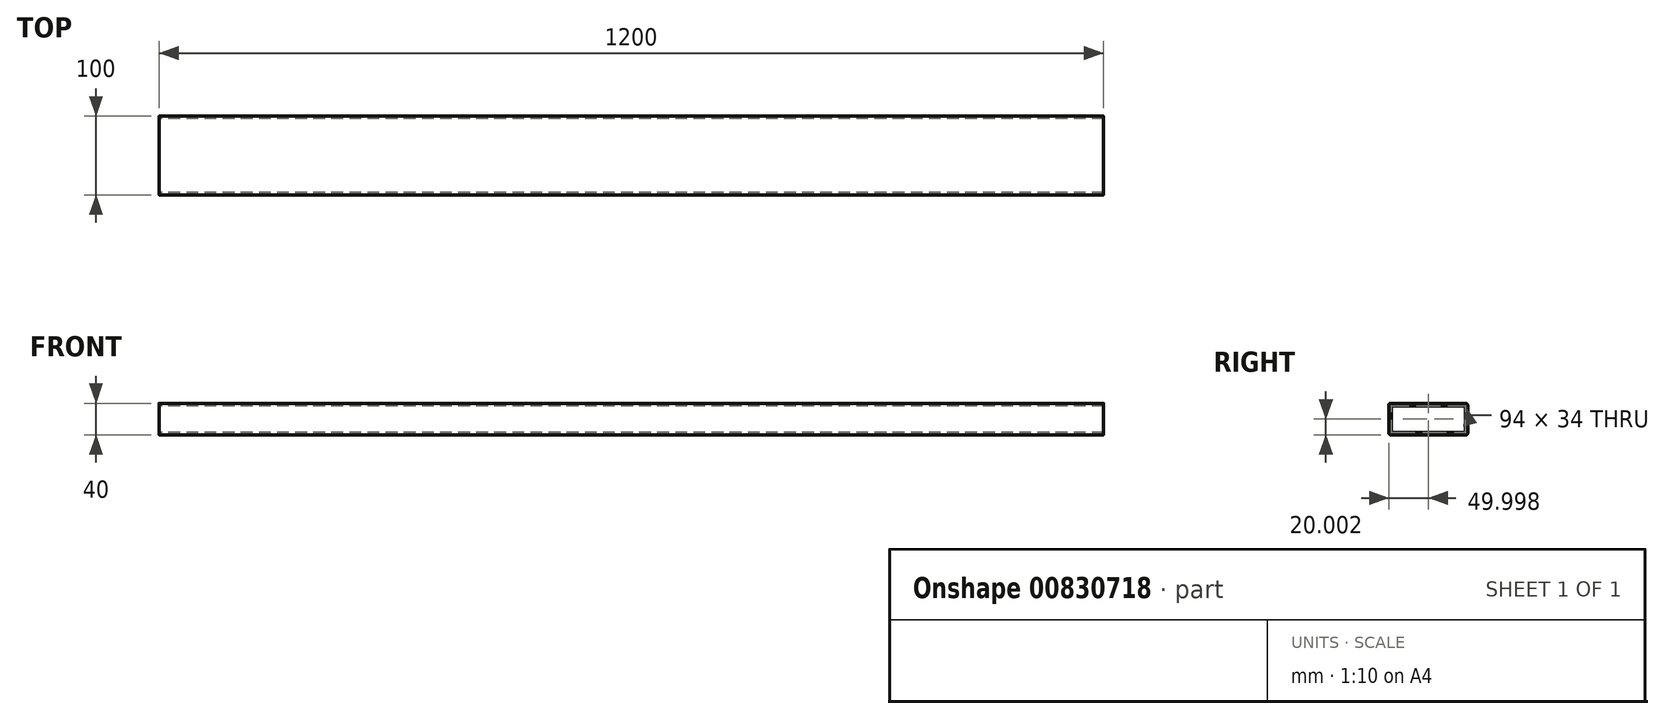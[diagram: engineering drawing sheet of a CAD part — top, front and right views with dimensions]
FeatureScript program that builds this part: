
annotation { "Feature Type Name" : "Feature", "Feature Type Description" : "" }
export const myFeature = defineFeature(function(context is Context, id is Id, definition is map)
    precondition{}
    {
        {
            assignVariable(context, id + "F0", {"name" : "LongSideSize", "anyValue" : 1200});
        }
        {
            var Q0;
            Q0=qCreatedBy(makeId("Right.planeOp"),FACE);
            var sketch = newSketch(context, id + "F1", { "sketchPlane" : qUnion([Q0])});
            skPoint(sketch, "E0.middle", {"position": v(-14.96, 34.76) * mm});
            skLineSegment(sketch, "E1.bottom", {"start": v(-17.25, -51.74) * mm, "end": v(78.75, -51.74) * mm});
            skLineSegment(sketch, "E1.top", {"start": v(-17.25, -11.74) * mm, "end": v(78.75, -11.74) * mm});
            skLineSegment(sketch, "E1.left", {"start": v(-19.25, -49.74) * mm, "end": v(-19.25, -13.74) * mm});
            skLineSegment(sketch, "E1.right", {"start": v(80.75, -49.74) * mm, "end": v(80.75, -13.74) * mm});
            skPoint(sketch, "E2.visualSharp", {"position": v(-19.25, -11.74) * mm});
            skArc(sketch, "E2.filletArc", {"start": v(-17.25, -11.74) * mm, "mid": v(-18.67, -12.32) * mm, "end": v(-19.25, -13.74) * mm});
            skPoint(sketch, "E3.visualSharp", {"position": v(80.75, -11.74) * mm});
            skArc(sketch, "E3.filletArc", {"start": v(80.75, -13.74) * mm, "mid": v(80.16, -12.32) * mm, "end": v(78.75, -11.74) * mm});
            skPoint(sketch, "E4.visualSharp", {"position": v(80.75, -51.74) * mm});
            skArc(sketch, "E4.filletArc", {"start": v(78.75, -51.74) * mm, "mid": v(80.16, -51.15) * mm, "end": v(80.75, -49.74) * mm});
            skPoint(sketch, "E5.visualSharp", {"position": v(-19.25, -51.74) * mm});
            skArc(sketch, "E5.filletArc", {"start": v(-19.25, -49.74) * mm, "mid": v(-18.67, -51.15) * mm, "end": v(-17.25, -51.74) * mm});
            skLineSegment(sketch, "E6.0", {"start": v(-17.25, 46.26) * mm, "end": v(-17.25, 46.26) * mm});
            skLineSegment(sketch, "E6.2", {"start": v(-17.25, -49.74) * mm, "end": v(-17.25, -49.74) * mm});
            skLineSegment(sketch, "E6.4", {"start": v(18.75, -49.74) * mm, "end": v(18.75, -49.74) * mm});
            skLineSegment(sketch, "E6.7", {"start": v(18.75, 46.26) * mm, "end": v(18.75, 46.26) * mm});
            skLineSegment(sketch, "E7.0", {"start": v(77.75, -48.74) * mm, "end": v(77.75, -14.74) * mm});
            skLineSegment(sketch, "E7.1", {"start": v(-16.25, -48.74) * mm, "end": v(77.75, -48.74) * mm});
            skLineSegment(sketch, "E7.2", {"start": v(-16.25, -48.74) * mm, "end": v(-16.25, -14.74) * mm});
            skLineSegment(sketch, "E7.3", {"start": v(-16.25, -14.74) * mm, "end": v(77.75, -14.74) * mm});
            skSolve(sketch);
        }
        {
            var Q0;
            Q0=qSketchRegion(id+"F1",true);
            extrude(context, id + "F2", {"entities" : qUnion([Q0]), "endBound" : BoundingType.SYMMETRIC, "depth" : (getVariable(context, 'LongSideSize')) * mm, "offsetDistance" : 25 * mm});
        }
        {
            var Q0;
            Q0=makeQuery(id+"F2.opExtrude","SWEPT_BODY",BODY,{"disambiguationData":[OSD([sQuery(id+"F1.wireOp",EDGE,"E1.bottom"),sQuery(id+"F1.wireOp",EDGE,"E1.top"),sQuery(id+"F1.wireOp",EDGE,"E1.left"),sQuery(id+"F1.wireOp",EDGE,"E1.right"),sQuery(id+"F1.wireOp",EDGE,"E2.filletArc"),sQuery(id+"F1.wireOp",EDGE,"E3.filletArc"),sQuery(id+"F1.wireOp",EDGE,"E4.filletArc"),sQuery(id+"F1.wireOp",EDGE,"E5.filletArc"),sQuery(id+"F1.wireOp",EDGE,"E7.0"),sQuery(id+"F1.wireOp",EDGE,"E7.1"),sQuery(id+"F1.wireOp",EDGE,"E7.2"),sQuery(id+"F1.wireOp",EDGE,"E7.3")])]});
            transform(context, id + "F3", {"entities" : qUnion([Q0]), "transformType" : TransformType.TRANSLATION_3D, "dx" : 0 * mm, "dy" : 0 * mm, "dz" : 0 * mm, "makeCopy" : true});
        }
        {
            var Q0;
            Q0=makeQuery(id+"F3.opPattern","COPY",BODY,{"derivedFrom":makeQuery(id+"F2.opExtrude","SWEPT_BODY",BODY,{"disambiguationData":[OSD([sQuery(id+"F1.wireOp",EDGE,"E1.bottom"),sQuery(id+"F1.wireOp",EDGE,"E1.top"),sQuery(id+"F1.wireOp",EDGE,"E1.left"),sQuery(id+"F1.wireOp",EDGE,"E1.right"),sQuery(id+"F1.wireOp",EDGE,"E2.filletArc"),sQuery(id+"F1.wireOp",EDGE,"E3.filletArc"),sQuery(id+"F1.wireOp",EDGE,"E4.filletArc"),sQuery(id+"F1.wireOp",EDGE,"E5.filletArc"),sQuery(id+"F1.wireOp",EDGE,"E7.0"),sQuery(id+"F1.wireOp",EDGE,"E7.1"),sQuery(id+"F1.wireOp",EDGE,"E7.2"),sQuery(id+"F1.wireOp",EDGE,"E7.3")])]}),"instanceName":"1"});
            deleteBodies(context, id + "F4", {"entities" : qUnion([Q0])});
        }
    });
